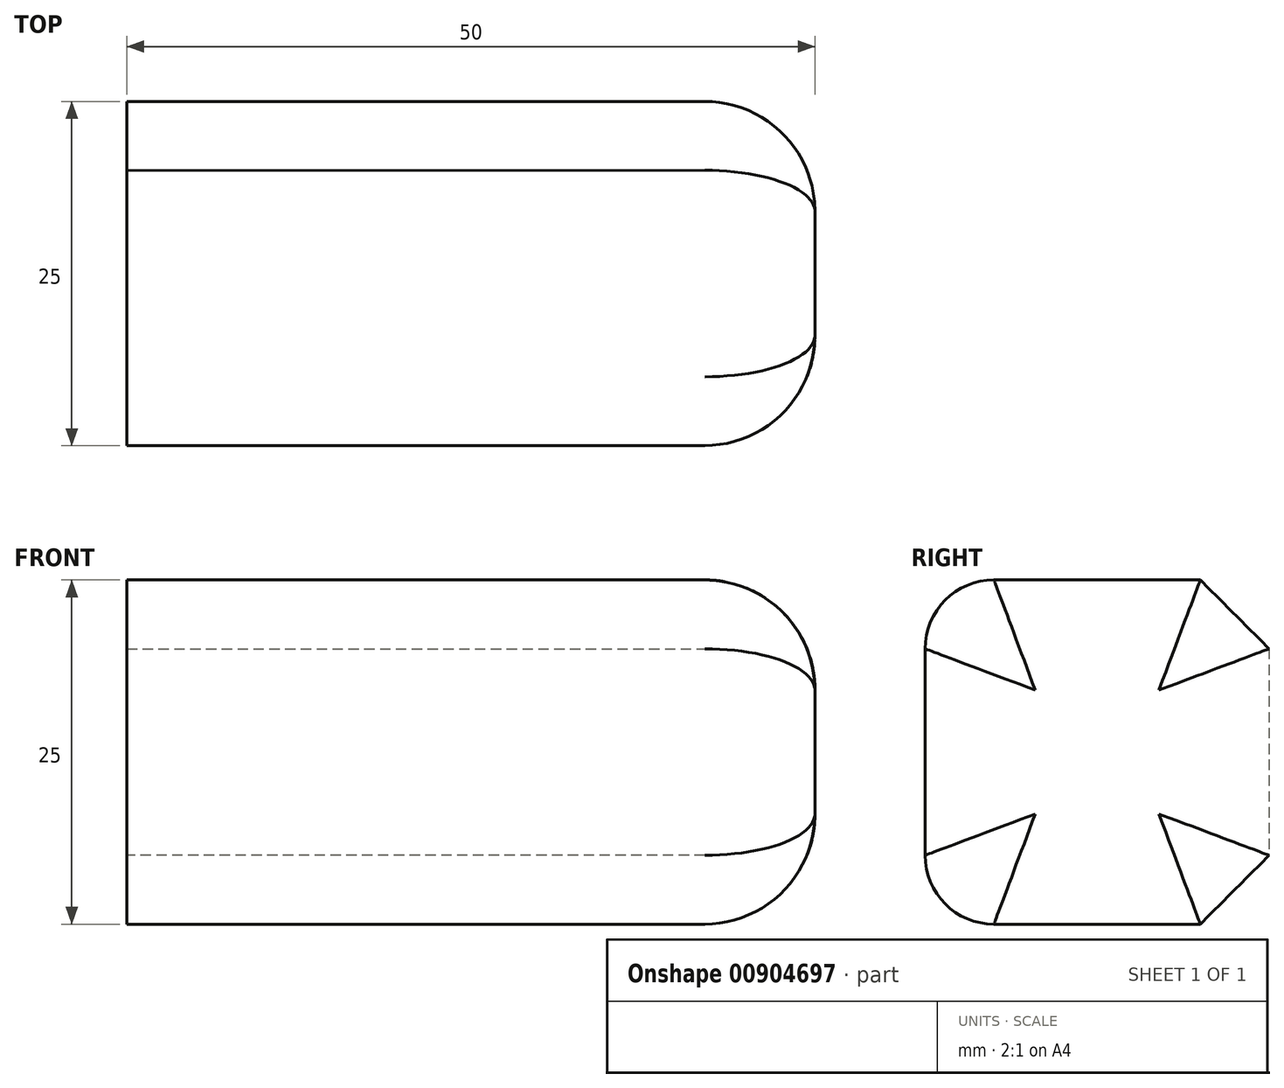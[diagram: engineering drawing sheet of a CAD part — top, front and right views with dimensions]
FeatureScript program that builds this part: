
annotation { "Feature Type Name" : "Feature", "Feature Type Description" : "" }
export const myFeature = defineFeature(function(context is Context, id is Id, definition is map)
    precondition{}
    {
        {
            var Q0;
            Q0=qCreatedBy(makeId("Top.planeOp"),FACE);
            var sketch = newSketch(context, id + "F0", { "sketchPlane" : qUnion([Q0])});
            skLineSegment(sketch, "E0", {"start": v(-20.58, 15.43) * mm, "end": v(-20.58, -9.55) * mm});
            skLineSegment(sketch, "E1", {"start": v(-20.58, -9.55) * mm, "end": v(29.42, -9.55) * mm});
            skLineSegment(sketch, "E2", {"start": v(29.42, -9.55) * mm, "end": v(29.42, 15.45) * mm});
            skLineSegment(sketch, "E3", {"start": v(29.42, 15.45) * mm, "end": v(-20.58, 15.43) * mm});
            skSolve(sketch);
        }
        {
            var Q0;
            Q0 = qSketchRegion(id + "F0", true);
            extrude(context, id + "F1", {"entities" : qUnion([Q0]), "depth" : 25 * mm, "offsetDistance" : 25 * mm});
        }
        {
            var Q0;
            Q0=makeQuery(id+"F1.opExtrude","SWEPT_EDGE",EDGE,{"disambiguationData":[OSD([sQuery(id+"F0.wireOp",EDGE,"E2"),sQuery(id+"F0.wireOp",EDGE,"E3")])]});
            var Q1;
            Q1=makeQuery(id+"F1.opExtrude","SWEPT_EDGE",EDGE,{"disambiguationData":[OSD([sQuery(id+"F0.wireOp",EDGE,"E1"),sQuery(id+"F0.wireOp",EDGE,"E2")])]});
            var Q2;
            Q2=makeQuery(id+"F1.opExtrude","CAP_EDGE",EDGE,{"disambiguationData":[OSD([sQuery(id+"F0.wireOp",EDGE,"E2")])],"isStart":false});
            var Q3;
            Q3=makeQuery(id+"F1.opExtrude","CAP_EDGE",EDGE,{"disambiguationData":[OSD([sQuery(id+"F0.wireOp",EDGE,"E2")])],"isStart":true});
            fillet(context, id + "F2", {"entities" : qUnion([Q0, Q1, Q2, Q3]), "tangentPropagation" : true, "radius" : 8 * mm, "defaultsChanged" : true, "vertexSettings" : [], "allowEdgeOverflow" : false});
        }
        {
            var Q0;
            Q0=makeQuery(id+"F1.opExtrude","CAP_EDGE",EDGE,{"disambiguationData":[OSD([sQuery(id+"F0.wireOp",EDGE,"E3")])],"isStart":false});
            var Q1;
            Q1=makeQuery(id+"F1.opExtrude","CAP_EDGE",EDGE,{"disambiguationData":[OSD([sQuery(id+"F0.wireOp",EDGE,"E3")])],"isStart":true});
            chamfer(context, id + "F3", {"entities" : qUnion([Q0, Q1]), "width" : 5 * mm, "tangentPropagation" : true});
        }
        {
            var Q0;
            Q0=makeQuery(id+"F1.opExtrude","CAP_EDGE",EDGE,{"disambiguationData":[OSD([sQuery(id+"F0.wireOp",EDGE,"E1")])],"isStart":true});
            var Q1;
            Q1=makeQuery(id+"F1.opExtrude","CAP_EDGE",EDGE,{"disambiguationData":[OSD([sQuery(id+"F0.wireOp",EDGE,"E1")])],"isStart":false});
            fillet(context, id + "F4", {"entities" : qUnion([Q0, Q1]), "tangentPropagation" : true, "radius" : 5 * mm, "defaultsChanged" : false, "vertexSettings" : [], "allowEdgeOverflow" : false});
        }
    });
